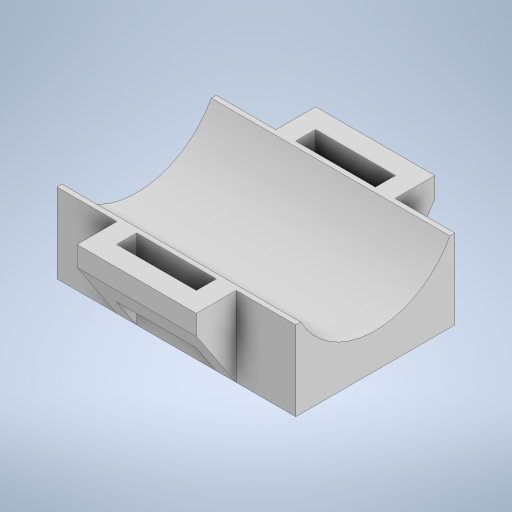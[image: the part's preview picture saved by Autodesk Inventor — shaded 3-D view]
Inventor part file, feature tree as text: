
AUTODESK INVENTOR PART (.ipt)
format: ipt  version: 2023 (Build 270158000, 158)  size: 292,352 bytes
history: native  units: in
note: dims shown in document units (in); Inventor stores cm internally (conversion verified against a paired STEP export)
features: extrude x4, sketch x4, projected_geometry x4, mirror x1
ambient origin geometry x8: Origin, YZ Plane, XZ Plane, XY Plane, X Axis, Y Axis, Z Axis, Center Point
bodies: Solid1 (feature_tree)
feature tree (13):
  extrude  "Extrusion1"  Depth=3.0in
  extrude  "Extrusion2"  Depth=1.5in
  extrude  "Extrusion3"  Depth=1.0in
  extrude  "Extrusion4"  Depth=1.0in
  mirror  "Mirror1"
  sketch  "Sketch1"  dims[d0=2.0in d1=3.0in]
  sketch  "Sketch2"  dims[d2=1.0in d3=1.5in]
  projected_geometry  "Projected Loop1"
  sketch  "Sketch3"  dims[d4=1.0in d5=0.0in d6=2.125in]
  projected_geometry  "Projected Loop2"
  sketch  "Sketch4"  dims[d7=1.0in d8=0.0in d10=1.0in d11=0.25in d12=0.25in d13=0.25in d14=0.25in d16=0.5in d17=1.0in d18=0.0in d19=0.25in d20=0.0in d21=0.0in]
  projected_geometry  "Projected Loop3"
  projected_geometry  "Projected Loop4"
